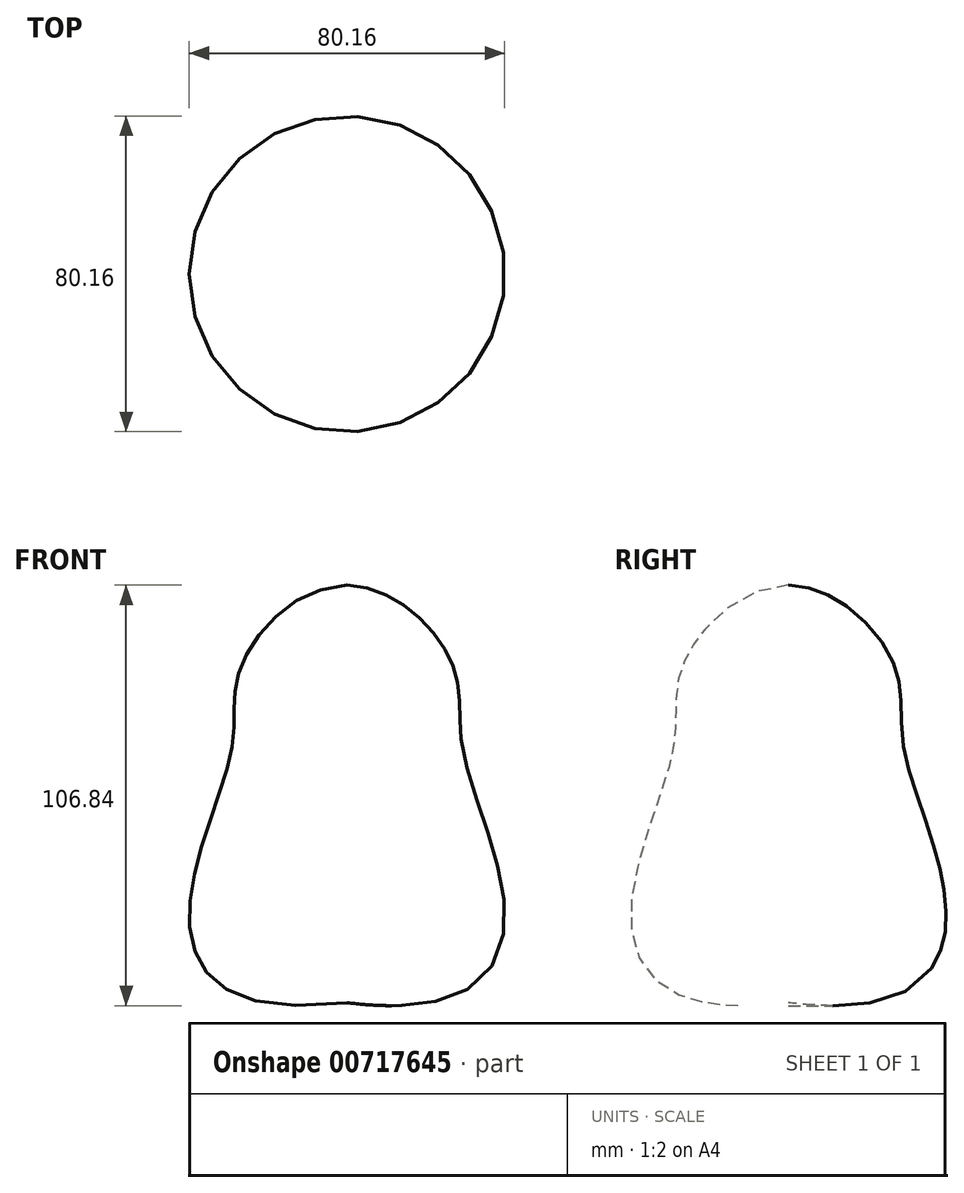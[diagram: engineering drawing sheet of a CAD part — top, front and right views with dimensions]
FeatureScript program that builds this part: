
annotation { "Feature Type Name" : "Feature", "Feature Type Description" : "" }
export const myFeature = defineFeature(function(context is Context, id is Id, definition is map)
    precondition{}
    {
        {
            var Q0;
            Q0=qCreatedBy(makeId("Front.planeOp"),FACE);
            var sketch = newSketch(context, id + "F0", { "sketchPlane" : qUnion([Q0])});
            skFitSpline(sketch, "E0", {"points": [v(0, 53.73) * mm, v(-27.03, 32.9) * mm, v(-29.28, 12.35) * mm, v(-40.06, -29.28) * mm, v(0, -52.35) * mm], "startDerivative": vector(-160.2, -4.95) * mm, "endDerivative": vector(337.91, 41.74) * mm});
            skLineSegment(sketch, "E1", {"start": v(0, 53.73) * mm, "end": v(0, -52.35) * mm});
            skSolve(sketch);
        }
        {
            var Q0;
            Q0 = qSketchRegion(id + "F0", true);
            var Q1;
            Q1=sQuery(id+"F0.wireOp",EDGE,"E1");
            revolve(context, id + "F1", {"surfaceOperationType" : NewSurfaceOperationType.NEW, "entities" : qUnion([Q0]), "axis" : qUnion([Q1]), "revolveType" : RevolveType.FULL});
        }
    });
